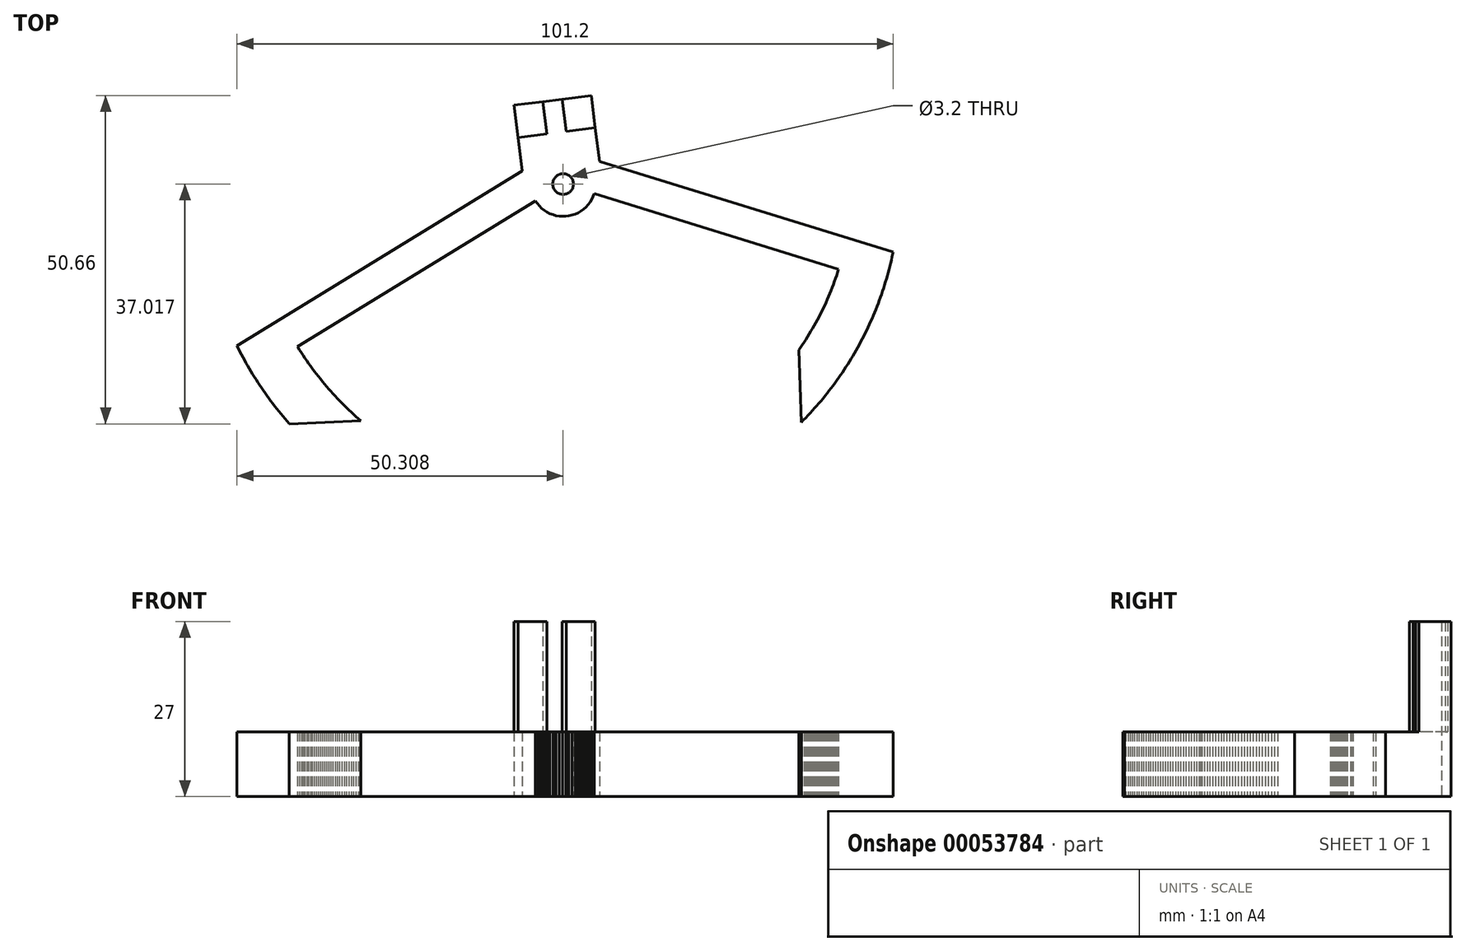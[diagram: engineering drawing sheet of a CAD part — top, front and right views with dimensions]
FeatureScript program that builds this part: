
annotation { "Feature Type Name" : "Feature", "Feature Type Description" : "" }
export const myFeature = defineFeature(function(context is Context, id is Id, definition is map)
    precondition{}
    {
        {
            var Q0;
            Q0=qCreatedBy(makeId("Top.planeOp"),FACE);
            var sketch = newSketch(context, id + "F0", { "sketchPlane" : qUnion([Q0])});
            skLineSegment(sketch, "E0", {"start": v(-31.49, -20.52) * mm, "end": v(-31.87, -20.2) * mm});
            skLineSegment(sketch, "E1", {"start": v(-31.87, -20.2) * mm, "end": v(-32.24, -19.86) * mm});
            skLineSegment(sketch, "E2", {"start": v(-32.24, -19.86) * mm, "end": v(-32.61, -19.53) * mm});
            skLineSegment(sketch, "E3", {"start": v(-32.61, -19.53) * mm, "end": v(-32.98, -19.2) * mm});
            skLineSegment(sketch, "E4", {"start": v(-32.98, -19.2) * mm, "end": v(-33.35, -18.85) * mm});
            skLineSegment(sketch, "E5", {"start": v(-33.35, -18.85) * mm, "end": v(-33.7, -18.5) * mm});
            skLineSegment(sketch, "E6", {"start": v(-33.7, -18.5) * mm, "end": v(-34.07, -18.15) * mm});
            skLineSegment(sketch, "E7", {"start": v(-34.07, -18.15) * mm, "end": v(-34.42, -17.8) * mm});
            skLineSegment(sketch, "E8", {"start": v(-34.42, -17.8) * mm, "end": v(-34.77, -17.44) * mm});
            skLineSegment(sketch, "E9", {"start": v(-34.77, -17.44) * mm, "end": v(-35.12, -17.08) * mm});
            skLineSegment(sketch, "E10", {"start": v(-35.12, -17.08) * mm, "end": v(-35.46, -16.72) * mm});
            skLineSegment(sketch, "E11", {"start": v(-35.46, -16.72) * mm, "end": v(-35.8, -16.35) * mm});
            skLineSegment(sketch, "E12", {"start": v(-35.8, -16.35) * mm, "end": v(-36.13, -15.98) * mm});
            skLineSegment(sketch, "E13", {"start": v(-36.13, -15.98) * mm, "end": v(-36.46, -15.6) * mm});
            skLineSegment(sketch, "E14", {"start": v(-36.46, -15.6) * mm, "end": v(-36.79, -15.23) * mm});
            skLineSegment(sketch, "E15", {"start": v(-36.79, -15.23) * mm, "end": v(-37.11, -14.84) * mm});
            skLineSegment(sketch, "E16", {"start": v(-37.11, -14.84) * mm, "end": v(-37.43, -14.46) * mm});
            skLineSegment(sketch, "E17", {"start": v(-37.43, -14.46) * mm, "end": v(-37.75, -14.07) * mm});
            skLineSegment(sketch, "E18", {"start": v(-37.75, -14.07) * mm, "end": v(-38.06, -13.68) * mm});
            skLineSegment(sketch, "E19", {"start": v(-38.06, -13.68) * mm, "end": v(-38.37, -13.28) * mm});
            skLineSegment(sketch, "E20", {"start": v(-38.37, -13.28) * mm, "end": v(-38.67, -12.89) * mm});
            skLineSegment(sketch, "E21", {"start": v(-38.67, -12.89) * mm, "end": v(-38.97, -12.49) * mm});
            skLineSegment(sketch, "E22", {"start": v(-38.97, -12.49) * mm, "end": v(-39.26, -12.08) * mm});
            skLineSegment(sketch, "E23", {"start": v(-39.26, -12.08) * mm, "end": v(-39.55, -11.67) * mm});
            skLineSegment(sketch, "E24", {"start": v(-39.55, -11.67) * mm, "end": v(-39.84, -11.26) * mm});
            skLineSegment(sketch, "E25", {"start": v(-39.84, -11.26) * mm, "end": v(-40.12, -10.85) * mm});
            skLineSegment(sketch, "E26", {"start": v(-40.12, -10.85) * mm, "end": v(-40.4, -10.44) * mm});
            skLineSegment(sketch, "E27", {"start": v(-40.4, -10.44) * mm, "end": v(-40.67, -10.02) * mm});
            skLineSegment(sketch, "E28", {"start": v(-40.67, -10.02) * mm, "end": v(-40.94, -9.6) * mm});
            skLineSegment(sketch, "E29", {"start": v(-40.94, -9.6) * mm, "end": v(-41.2, -9.17) * mm});
            skLineSegment(sketch, "E30", {"start": v(-41.2, -9.17) * mm, "end": v(-41.25, -9.1) * mm});
            skLineSegment(sketch, "E31", {"start": v(-41.25, -9.1) * mm, "end": v(-4.56, 13.4) * mm});
            skLineSegment(sketch, "E32", {"start": v(-4.56, 13.4) * mm, "end": v(-4.27, 12.98) * mm});
            skLineSegment(sketch, "E33", {"start": v(-4.27, 12.98) * mm, "end": v(-3.95, 12.6) * mm});
            skLineSegment(sketch, "E34", {"start": v(-3.95, 12.6) * mm, "end": v(-3.6, 12.25) * mm});
            skLineSegment(sketch, "E35", {"start": v(-3.6, 12.25) * mm, "end": v(-3.2, 11.94) * mm});
            skLineSegment(sketch, "E36", {"start": v(-3.2, 11.94) * mm, "end": v(-2.78, 11.67) * mm});
            skLineSegment(sketch, "E37", {"start": v(-2.78, 11.67) * mm, "end": v(-2.34, 11.44) * mm});
            skLineSegment(sketch, "E38", {"start": v(-2.34, 11.44) * mm, "end": v(-1.87, 11.26) * mm});
            skLineSegment(sketch, "E39", {"start": v(-1.87, 11.26) * mm, "end": v(-1.39, 11.13) * mm});
            skLineSegment(sketch, "E40", {"start": v(-1.39, 11.13) * mm, "end": v(-0.9, 11.04) * mm});
            skLineSegment(sketch, "E41", {"start": v(-0.9, 11.04) * mm, "end": v(-0.4, 11) * mm});
            skLineSegment(sketch, "E42", {"start": v(-0.4, 11) * mm, "end": v(0.1, 11.02) * mm});
            skLineSegment(sketch, "E43", {"start": v(0.1, 11.02) * mm, "end": v(0.6, 11.09) * mm});
            skLineSegment(sketch, "E44", {"start": v(0.6, 11.09) * mm, "end": v(1.08, 11.2) * mm});
            skLineSegment(sketch, "E45", {"start": v(1.08, 11.2) * mm, "end": v(1.56, 11.36) * mm});
            skLineSegment(sketch, "E46", {"start": v(1.56, 11.36) * mm, "end": v(2.01, 11.57) * mm});
            skLineSegment(sketch, "E47", {"start": v(2.01, 11.57) * mm, "end": v(2.44, 11.82) * mm});
            skLineSegment(sketch, "E48", {"start": v(2.44, 11.82) * mm, "end": v(2.85, 12.12) * mm});
            skLineSegment(sketch, "E49", {"start": v(2.85, 12.12) * mm, "end": v(3.22, 12.45) * mm});
            skLineSegment(sketch, "E50", {"start": v(3.22, 12.45) * mm, "end": v(3.56, 12.82) * mm});
            skLineSegment(sketch, "E51", {"start": v(3.56, 12.82) * mm, "end": v(3.86, 13.22) * mm});
            skLineSegment(sketch, "E52", {"start": v(3.86, 13.22) * mm, "end": v(4.12, 13.65) * mm});
            skLineSegment(sketch, "E53", {"start": v(4.12, 13.65) * mm, "end": v(4.33, 14.1) * mm});
            skLineSegment(sketch, "E54", {"start": v(4.33, 14.1) * mm, "end": v(4.48, 14.53) * mm});
            skLineSegment(sketch, "E55", {"start": v(4.48, 14.53) * mm, "end": v(42.19, 2.87) * mm});
            skLineSegment(sketch, "E56", {"start": v(42.19, 2.87) * mm, "end": v(42.04, 2.39) * mm});
            skLineSegment(sketch, "E57", {"start": v(42.04, 2.39) * mm, "end": v(41.88, 1.91) * mm});
            skLineSegment(sketch, "E58", {"start": v(41.88, 1.91) * mm, "end": v(41.72, 1.44) * mm});
            skLineSegment(sketch, "E59", {"start": v(41.72, 1.44) * mm, "end": v(41.55, 0.97) * mm});
            skLineSegment(sketch, "E60", {"start": v(41.55, 0.97) * mm, "end": v(41.38, 0.5) * mm});
            skLineSegment(sketch, "E61", {"start": v(41.38, 0.5) * mm, "end": v(41.2, 0.03) * mm});
            skLineSegment(sketch, "E62", {"start": v(41.2, 0.03) * mm, "end": v(41.02, -0.43) * mm});
            skLineSegment(sketch, "E63", {"start": v(41.02, -0.43) * mm, "end": v(40.83, -0.9) * mm});
            skLineSegment(sketch, "E64", {"start": v(40.83, -0.9) * mm, "end": v(40.64, -1.36) * mm});
            skLineSegment(sketch, "E65", {"start": v(40.64, -1.36) * mm, "end": v(40.44, -1.82) * mm});
            skLineSegment(sketch, "E66", {"start": v(40.44, -1.82) * mm, "end": v(40.24, -2.27) * mm});
            skLineSegment(sketch, "E67", {"start": v(40.24, -2.27) * mm, "end": v(40.03, -2.73) * mm});
            skLineSegment(sketch, "E68", {"start": v(40.03, -2.73) * mm, "end": v(39.82, -3.18) * mm});
            skLineSegment(sketch, "E69", {"start": v(39.82, -3.18) * mm, "end": v(39.6, -3.63) * mm});
            skLineSegment(sketch, "E70", {"start": v(39.6, -3.63) * mm, "end": v(39.38, -4.08) * mm});
            skLineSegment(sketch, "E71", {"start": v(39.38, -4.08) * mm, "end": v(39.15, -4.52) * mm});
            skLineSegment(sketch, "E72", {"start": v(39.15, -4.52) * mm, "end": v(38.92, -4.97) * mm});
            skLineSegment(sketch, "E73", {"start": v(38.92, -4.97) * mm, "end": v(38.68, -5.4) * mm});
            skLineSegment(sketch, "E74", {"start": v(38.68, -5.4) * mm, "end": v(38.43, -5.84) * mm});
            skLineSegment(sketch, "E75", {"start": v(38.43, -5.84) * mm, "end": v(38.19, -6.28) * mm});
            skLineSegment(sketch, "E76", {"start": v(38.19, -6.28) * mm, "end": v(37.93, -6.7) * mm});
            skLineSegment(sketch, "E77", {"start": v(37.93, -6.7) * mm, "end": v(37.68, -7.14) * mm});
            skLineSegment(sketch, "E78", {"start": v(37.68, -7.14) * mm, "end": v(37.41, -7.56) * mm});
            skLineSegment(sketch, "E79", {"start": v(37.41, -7.56) * mm, "end": v(37.15, -7.98) * mm});
            skLineSegment(sketch, "E80", {"start": v(37.15, -7.98) * mm, "end": v(36.87, -8.4) * mm});
            skLineSegment(sketch, "E81", {"start": v(36.87, -8.4) * mm, "end": v(36.6, -8.82) * mm});
            skLineSegment(sketch, "E82", {"start": v(36.6, -8.82) * mm, "end": v(36.32, -9.23) * mm});
            skLineSegment(sketch, "E83", {"start": v(36.32, -9.23) * mm, "end": v(36.05, -9.62) * mm});
            skLineSegment(sketch, "E84", {"start": v(36.05, -9.62) * mm, "end": v(36.42, -20.76) * mm});
            skLineSegment(sketch, "E85", {"start": v(36.42, -20.76) * mm, "end": v(36.78, -20.4) * mm});
            skLineSegment(sketch, "E86", {"start": v(36.78, -20.4) * mm, "end": v(37.12, -20.05) * mm});
            skLineSegment(sketch, "E87", {"start": v(37.12, -20.05) * mm, "end": v(37.47, -19.69) * mm});
            skLineSegment(sketch, "E88", {"start": v(37.47, -19.69) * mm, "end": v(37.81, -19.32) * mm});
            skLineSegment(sketch, "E89", {"start": v(37.81, -19.32) * mm, "end": v(38.15, -18.96) * mm});
            skLineSegment(sketch, "E90", {"start": v(38.15, -18.96) * mm, "end": v(38.48, -18.58) * mm});
            skLineSegment(sketch, "E91", {"start": v(38.48, -18.58) * mm, "end": v(38.82, -18.2) * mm});
            skLineSegment(sketch, "E92", {"start": v(38.82, -18.2) * mm, "end": v(39.14, -17.83) * mm});
            skLineSegment(sketch, "E93", {"start": v(39.14, -17.83) * mm, "end": v(39.47, -17.45) * mm});
            skLineSegment(sketch, "E94", {"start": v(39.47, -17.45) * mm, "end": v(39.79, -17.07) * mm});
            skLineSegment(sketch, "E95", {"start": v(39.79, -17.07) * mm, "end": v(40.1, -16.68) * mm});
            skLineSegment(sketch, "E96", {"start": v(40.1, -16.68) * mm, "end": v(40.42, -16.29) * mm});
            skLineSegment(sketch, "E97", {"start": v(40.42, -16.29) * mm, "end": v(40.72, -15.9) * mm});
            skLineSegment(sketch, "E98", {"start": v(40.72, -15.9) * mm, "end": v(41.03, -15.5) * mm});
            skLineSegment(sketch, "E99", {"start": v(41.03, -15.5) * mm, "end": v(41.33, -15.1) * mm});
            skLineSegment(sketch, "E100", {"start": v(41.33, -15.1) * mm, "end": v(41.63, -14.7) * mm});
            skLineSegment(sketch, "E101", {"start": v(41.63, -14.7) * mm, "end": v(41.92, -14.3) * mm});
            skLineSegment(sketch, "E102", {"start": v(41.92, -14.3) * mm, "end": v(42.21, -13.89) * mm});
            skLineSegment(sketch, "E103", {"start": v(42.21, -13.89) * mm, "end": v(42.5, -13.48) * mm});
            skLineSegment(sketch, "E104", {"start": v(42.5, -13.48) * mm, "end": v(42.78, -13.06) * mm});
            skLineSegment(sketch, "E105", {"start": v(42.78, -13.06) * mm, "end": v(43.06, -12.65) * mm});
            skLineSegment(sketch, "E106", {"start": v(43.06, -12.65) * mm, "end": v(43.33, -12.23) * mm});
            skLineSegment(sketch, "E107", {"start": v(43.33, -12.23) * mm, "end": v(43.6, -11.8) * mm});
            skLineSegment(sketch, "E108", {"start": v(43.6, -11.8) * mm, "end": v(43.87, -11.38) * mm});
            skLineSegment(sketch, "E109", {"start": v(43.87, -11.38) * mm, "end": v(44.13, -10.96) * mm});
            skLineSegment(sketch, "E110", {"start": v(44.13, -10.96) * mm, "end": v(44.38, -10.53) * mm});
            skLineSegment(sketch, "E111", {"start": v(44.38, -10.53) * mm, "end": v(44.64, -10.1) * mm});
            skLineSegment(sketch, "E112", {"start": v(44.64, -10.1) * mm, "end": v(44.89, -9.66) * mm});
            skLineSegment(sketch, "E113", {"start": v(44.89, -9.66) * mm, "end": v(45.13, -9.23) * mm});
            skLineSegment(sketch, "E114", {"start": v(45.13, -9.23) * mm, "end": v(45.37, -8.8) * mm});
            skLineSegment(sketch, "E115", {"start": v(45.37, -8.8) * mm, "end": v(45.6, -8.35) * mm});
            skLineSegment(sketch, "E116", {"start": v(45.6, -8.35) * mm, "end": v(45.84, -7.9) * mm});
            skLineSegment(sketch, "E117", {"start": v(45.84, -7.9) * mm, "end": v(46.07, -7.46) * mm});
            skLineSegment(sketch, "E118", {"start": v(46.07, -7.46) * mm, "end": v(46.3, -7.01) * mm});
            skLineSegment(sketch, "E119", {"start": v(46.3, -7.01) * mm, "end": v(46.51, -6.57) * mm});
            skLineSegment(sketch, "E120", {"start": v(46.51, -6.57) * mm, "end": v(46.73, -6.11) * mm});
            skLineSegment(sketch, "E121", {"start": v(46.73, -6.11) * mm, "end": v(46.94, -5.66) * mm});
            skLineSegment(sketch, "E122", {"start": v(46.94, -5.66) * mm, "end": v(47.14, -5.2) * mm});
            skLineSegment(sketch, "E123", {"start": v(47.14, -5.2) * mm, "end": v(47.35, -4.75) * mm});
            skLineSegment(sketch, "E124", {"start": v(47.35, -4.75) * mm, "end": v(47.54, -4.29) * mm});
            skLineSegment(sketch, "E125", {"start": v(47.54, -4.29) * mm, "end": v(47.74, -3.83) * mm});
            skLineSegment(sketch, "E126", {"start": v(47.74, -3.83) * mm, "end": v(47.93, -3.36) * mm});
            skLineSegment(sketch, "E127", {"start": v(47.93, -3.36) * mm, "end": v(48.1, -2.9) * mm});
            skLineSegment(sketch, "E128", {"start": v(48.1, -2.9) * mm, "end": v(48.29, -2.43) * mm});
            skLineSegment(sketch, "E129", {"start": v(48.29, -2.43) * mm, "end": v(48.46, -1.96) * mm});
            skLineSegment(sketch, "E130", {"start": v(48.46, -1.96) * mm, "end": v(48.64, -1.5) * mm});
            skLineSegment(sketch, "E131", {"start": v(48.64, -1.5) * mm, "end": v(48.8, -1.02) * mm});
            skLineSegment(sketch, "E132", {"start": v(48.8, -1.02) * mm, "end": v(48.96, -0.55) * mm});
            skLineSegment(sketch, "E133", {"start": v(48.96, -0.55) * mm, "end": v(49.12, -0.07) * mm});
            skLineSegment(sketch, "E134", {"start": v(49.12, -0.07) * mm, "end": v(49.27, 0.4) * mm});
            skLineSegment(sketch, "E135", {"start": v(49.27, 0.4) * mm, "end": v(49.42, 0.88) * mm});
            skLineSegment(sketch, "E136", {"start": v(49.42, 0.88) * mm, "end": v(49.56, 1.36) * mm});
            skLineSegment(sketch, "E137", {"start": v(49.56, 1.36) * mm, "end": v(49.7, 1.84) * mm});
            skLineSegment(sketch, "E138", {"start": v(49.7, 1.84) * mm, "end": v(49.84, 2.32) * mm});
            skLineSegment(sketch, "E139", {"start": v(49.84, 2.32) * mm, "end": v(49.97, 2.8) * mm});
            skLineSegment(sketch, "E140", {"start": v(49.97, 2.8) * mm, "end": v(50.1, 3.29) * mm});
            skLineSegment(sketch, "E141", {"start": v(50.1, 3.29) * mm, "end": v(50.21, 3.77) * mm});
            skLineSegment(sketch, "E142", {"start": v(50.21, 3.77) * mm, "end": v(50.33, 4.26) * mm});
            skLineSegment(sketch, "E143", {"start": v(50.33, 4.26) * mm, "end": v(50.44, 4.75) * mm});
            skLineSegment(sketch, "E144", {"start": v(50.44, 4.75) * mm, "end": v(50.54, 5.24) * mm});
            skLineSegment(sketch, "E145", {"start": v(50.54, 5.24) * mm, "end": v(50.6, 5.5) * mm});
            skLineSegment(sketch, "E146", {"start": v(50.6, 5.5) * mm, "end": v(1.19, 20.78) * mm});
            skLineSegment(sketch, "E147", {"start": v(1.19, 20.78) * mm, "end": v(0.7, 20.9) * mm});
            skLineSegment(sketch, "E148", {"start": v(0.7, 20.9) * mm, "end": v(0.2, 20.98) * mm});
            skLineSegment(sketch, "E149", {"start": v(0.2, 20.98) * mm, "end": v(-0.3, 21) * mm});
            skLineSegment(sketch, "E150", {"start": v(-0.3, 21) * mm, "end": v(-0.8, 20.98) * mm});
            skLineSegment(sketch, "E151", {"start": v(-0.8, 20.98) * mm, "end": v(-1.29, 20.9) * mm});
            skLineSegment(sketch, "E152", {"start": v(-1.29, 20.9) * mm, "end": v(-1.77, 20.78) * mm});
            skLineSegment(sketch, "E153", {"start": v(-1.77, 20.78) * mm, "end": v(-2.24, 20.61) * mm});
            skLineSegment(sketch, "E154", {"start": v(-2.24, 20.61) * mm, "end": v(-2.69, 20.4) * mm});
            skLineSegment(sketch, "E155", {"start": v(-2.69, 20.4) * mm, "end": v(-2.9, 20.27) * mm});
            skLineSegment(sketch, "E156", {"start": v(-2.9, 20.27) * mm, "end": v(-50.6, -8.96) * mm});
            skLineSegment(sketch, "E157", {"start": v(-50.6, -8.96) * mm, "end": v(-50.37, -9.4) * mm});
            skLineSegment(sketch, "E158", {"start": v(-50.37, -9.4) * mm, "end": v(-50.14, -9.85) * mm});
            skLineSegment(sketch, "E159", {"start": v(-50.14, -9.85) * mm, "end": v(-49.91, -10.3) * mm});
            skLineSegment(sketch, "E160", {"start": v(-49.91, -10.3) * mm, "end": v(-49.68, -10.73) * mm});
            skLineSegment(sketch, "E161", {"start": v(-49.68, -10.73) * mm, "end": v(-49.44, -11.17) * mm});
            skLineSegment(sketch, "E162", {"start": v(-49.44, -11.17) * mm, "end": v(-49.2, -11.6) * mm});
            skLineSegment(sketch, "E163", {"start": v(-49.2, -11.6) * mm, "end": v(-48.94, -12.04) * mm});
            skLineSegment(sketch, "E164", {"start": v(-48.94, -12.04) * mm, "end": v(-48.7, -12.47) * mm});
            skLineSegment(sketch, "E165", {"start": v(-48.7, -12.47) * mm, "end": v(-48.44, -12.9) * mm});
            skLineSegment(sketch, "E166", {"start": v(-48.44, -12.9) * mm, "end": v(-48.18, -13.33) * mm});
            skLineSegment(sketch, "E167", {"start": v(-48.18, -13.33) * mm, "end": v(-47.92, -13.76) * mm});
            skLineSegment(sketch, "E168", {"start": v(-47.92, -13.76) * mm, "end": v(-47.65, -14.18) * mm});
            skLineSegment(sketch, "E169", {"start": v(-47.65, -14.18) * mm, "end": v(-47.38, -14.6) * mm});
            skLineSegment(sketch, "E170", {"start": v(-47.38, -14.6) * mm, "end": v(-47.1, -15.02) * mm});
            skLineSegment(sketch, "E171", {"start": v(-47.1, -15.02) * mm, "end": v(-46.83, -15.43) * mm});
            skLineSegment(sketch, "E172", {"start": v(-46.83, -15.43) * mm, "end": v(-46.54, -15.85) * mm});
            skLineSegment(sketch, "E173", {"start": v(-46.54, -15.85) * mm, "end": v(-46.26, -16.26) * mm});
            skLineSegment(sketch, "E174", {"start": v(-46.26, -16.26) * mm, "end": v(-45.97, -16.66) * mm});
            skLineSegment(sketch, "E175", {"start": v(-45.97, -16.66) * mm, "end": v(-45.68, -17.07) * mm});
            skLineSegment(sketch, "E176", {"start": v(-45.68, -17.07) * mm, "end": v(-45.38, -17.47) * mm});
            skLineSegment(sketch, "E177", {"start": v(-45.38, -17.47) * mm, "end": v(-45.08, -17.87) * mm});
            skLineSegment(sketch, "E178", {"start": v(-45.08, -17.87) * mm, "end": v(-44.78, -18.27) * mm});
            skLineSegment(sketch, "E179", {"start": v(-44.78, -18.27) * mm, "end": v(-44.47, -18.66) * mm});
            skLineSegment(sketch, "E180", {"start": v(-44.47, -18.66) * mm, "end": v(-44.16, -19.06) * mm});
            skLineSegment(sketch, "E181", {"start": v(-44.16, -19.06) * mm, "end": v(-43.85, -19.45) * mm});
            skLineSegment(sketch, "E182", {"start": v(-43.85, -19.45) * mm, "end": v(-43.53, -19.83) * mm});
            skLineSegment(sketch, "E183", {"start": v(-43.53, -19.83) * mm, "end": v(-43.2, -20.22) * mm});
            skLineSegment(sketch, "E184", {"start": v(-43.2, -20.22) * mm, "end": v(-42.88, -20.6) * mm});
            skLineSegment(sketch, "E185", {"start": v(-42.88, -20.6) * mm, "end": v(-42.56, -20.97) * mm});
            skLineSegment(sketch, "E186", {"start": v(-42.56, -20.97) * mm, "end": v(-42.53, -21) * mm});
            skLineSegment(sketch, "E187", {"start": v(-42.53, -21) * mm, "end": v(-31.49, -20.52) * mm});
            skCircle(sketch, "E188", {"center": v(-0.3, 16) * mm, "radius": 1.6 * mm});
            skLineSegment(sketch, "E189", {"start": v(-4.56, 13.4) * mm, "end": v(4.48, 14.53) * mm, "construction": true});
            skLineSegment(sketch, "E190", {"start": v(-5.99, 13.21) * mm, "end": v(5.92, 14.7) * mm});
            skPoint(sketch, "E191", {"position": v(-0.04, 13.96) * mm});
            skLineSegment(sketch, "E192", {"start": v(5.92, 14.7) * mm, "end": v(4.04, 29.65) * mm});
            skLineSegment(sketch, "E193", {"start": v(-5.99, 13.21) * mm, "end": v(-7.86, 28.16) * mm});
            skLineSegment(sketch, "E194", {"start": v(-7.86, 28.16) * mm, "end": v(4.04, 29.65) * mm});
            skLineSegment(sketch, "E195", {"start": v(-6.25, 15.26) * mm, "end": v(5.66, 16.75) * mm, "construction": true});
            skLineSegment(sketch, "E196", {"start": v(-21.17, 0) * mm, "end": v(21.98, 0) * mm, "construction": true});
            skLineSegment(sketch, "E197", {"start": v(-0.04, 13.96) * mm, "end": v(-1.91, 28.9) * mm, "construction": true});
            skLineSegment(sketch, "E198", {"start": v(-7.24, 23.2) * mm, "end": v(4.66, 24.7) * mm});
            skLineSegment(sketch, "E199", {"start": v(-3.4, 28.72) * mm, "end": v(-2.78, 23.76) * mm});
            skLineSegment(sketch, "E200", {"start": v(-0.42, 29.1) * mm, "end": v(0.2, 24.13) * mm});
            skLineSegment(sketch, "E201", {"start": v(-68.01, 37.38) * mm, "end": v(-68.01, 52.44) * mm, "construction": true});
            skCircle(sketch, "E202", {"center": v(-68.01, 39.44) * mm, "radius": 1.6 * mm});
            skLineSegment(sketch, "E203", {"start": v(-74.01, 47.44) * mm, "end": v(-62.01, 47.44) * mm});
            skLineSegment(sketch, "E204", {"start": v(-69.51, 52.44) * mm, "end": v(-69.51, 47.44) * mm});
            skLineSegment(sketch, "E205", {"start": v(-62.01, 37.38) * mm, "end": v(-62.01, 52.44) * mm});
            skLineSegment(sketch, "E206", {"start": v(-74.01, 37.38) * mm, "end": v(-74.01, 52.44) * mm});
            skLineSegment(sketch, "E207", {"start": v(-66.51, 52.44) * mm, "end": v(-66.51, 47.44) * mm});
            skLineSegment(sketch, "E208", {"start": v(-74.01, 52.44) * mm, "end": v(-62.01, 52.44) * mm});
            skPoint(sketch, "E201.startSnap0", {"position": v(-68.01, 37.38) * mm});
            skLineSegment(sketch, "E209", {"start": v(-74.01, 39.44) * mm, "end": v(-62.01, 39.44) * mm, "construction": true});
            skLineSegment(sketch, "E210", {"start": v(-74.01, 37.38) * mm, "end": v(-62.01, 37.38) * mm});
            skLineSegment(sketch, "E211", {"start": v(-72.57, 37.38) * mm, "end": v(-63.46, 37.38) * mm, "construction": true});
            skSolve(sketch);
        }
        {
            var Q0;
            {var subQ1=sQuery(id+"F0.wireOp",EDGE,"E147");Q0=makeQuery(id+"F0.imprint","IMPRINT",FACE,{"disambiguationData":[TD([[makeQuery(id+"F0.imprint","IMPRINT",EDGE,{"derivedFrom":subQ1}),-1.0]])]});}
            var Q1;
            {var subQ1=sQuery(id+"F0.wireOp",EDGE,"E147");Q1=makeQuery(id+"F0.imprint","IMPRINT",FACE,{"disambiguationData":[TD([[makeQuery(id+"F0.imprint","IMPRINT",EDGE,{"derivedFrom":subQ1}),1.0]])]});}
            var Q2;
            Q2=makeQuery(id+"F0.imprint","IMPRINT",FACE,{"disambiguationData":[TD([[makeQuery(id+"F0.imprint","IMPRINT",EDGE,{"derivedFrom":sQuery(id+"F0.wireOp",EDGE,"E0")}),1.0]])]});
            var Q3;
            {var subQ1=sQuery(id+"F0.wireOp",EDGE,"E32");Q3=makeQuery(id+"F0.imprint","IMPRINT",FACE,{"disambiguationData":[TD([[makeQuery(id+"F0.imprint","IMPRINT",EDGE,{"derivedFrom":subQ1}),1.0]])]});}
            var Q4;
            {var subQ0=sQuery(id+"F0.wireOp",EDGE,"E55");Q4=makeQuery(id+"F0.imprint","IMPRINT",FACE,{"disambiguationData":[TD([[makeQuery(id+"F0.imprint","IMPRINT",EDGE,{"derivedFrom":subQ0}),1.0]])]});}
            var Q5;
            {var subQ0=sQuery(id+"F0.wireOp",EDGE,"E199");Q5=makeQuery(id+"F0.imprint","IMPRINT",FACE,{"disambiguationData":[TD([[makeQuery(id+"F0.imprint","IMPRINT",EDGE,{"derivedFrom":subQ0}),1.0]])]});}
            extrude(context, id + "F1", {"entities" : qUnion([Q0, Q1, Q2, Q3, Q4, Q5]), "depth" : 10 * mm});
        }
        {
            var Q0;
            {var subQ5=sQuery(id+"F0.wireOp",EDGE,"E199");Q0=makeQuery(id+"F0.imprint","IMPRINT",FACE,{"disambiguationData":[TD([[makeQuery(id+"F0.imprint","IMPRINT",EDGE,{"derivedFrom":subQ5}),-1.0]])]});}
            var Q1;
            {var subQ5=sQuery(id+"F0.wireOp",EDGE,"E200");Q1=makeQuery(id+"F0.imprint","IMPRINT",FACE,{"disambiguationData":[TD([[makeQuery(id+"F0.imprint","IMPRINT",EDGE,{"derivedFrom":subQ5}),1.0]])]});}
            extrude(context, id + "F2", {"entities" : qUnion([Q0, Q1]), "operationType" : NewBodyOperationType.ADD, "depth" : 27 * mm});
        }
    });
